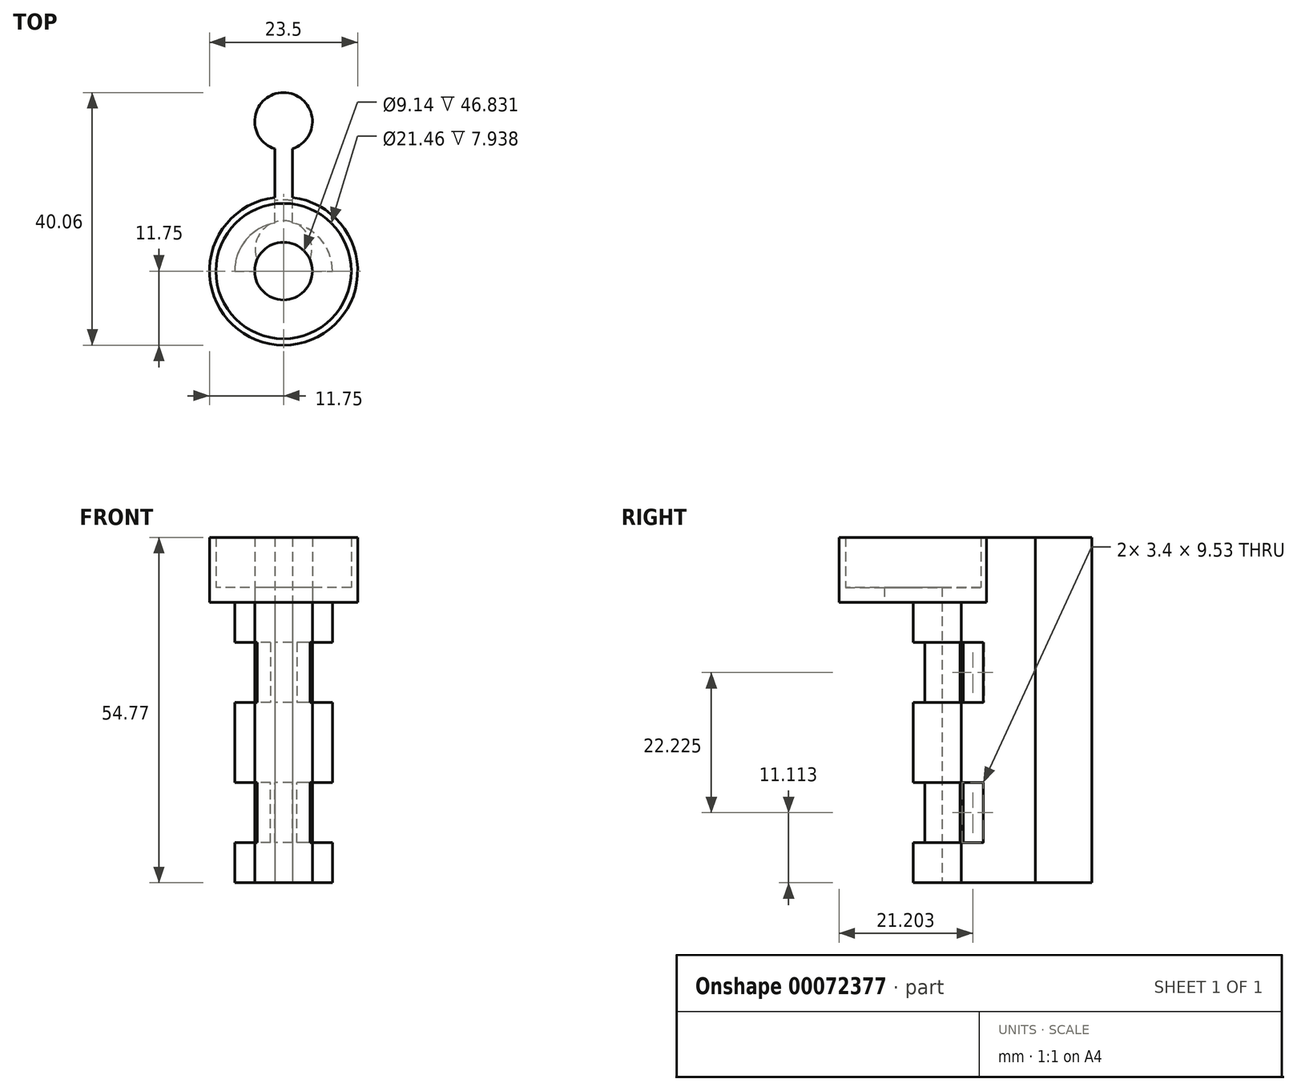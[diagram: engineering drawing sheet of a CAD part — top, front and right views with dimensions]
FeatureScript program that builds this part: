
annotation { "Feature Type Name" : "Feature", "Feature Type Description" : "" }
export const myFeature = defineFeature(function(context is Context, id is Id, definition is map)
    precondition{}
    {
        {
            var Q0;
            Q0=qCreatedBy(makeId("Top.planeOp"),FACE);
            var sketch = newSketch(context, id + "F0", { "sketchPlane" : qUnion([Q0])});
            skArc(sketch, "E0", {"start": v(4.57, 0) * mm, "mid": v(0, 4.57) * mm, "end": v(-4.57, 0) * mm});
            skArc(sketch, "E1", {"start": v(7.75, 0) * mm, "mid": v(0, 7.75) * mm, "end": v(-7.75, 0) * mm});
            skLineSegment(sketch, "E2", {"start": v(-7.75, 0) * mm, "end": v(-4.57, 0) * mm});
            skLineSegment(sketch, "E3", {"start": v(4.57, 0) * mm, "end": v(7.75, 0) * mm});
            skCircle(sketch, "E4", {"center": v(0, 23.73) * mm, "radius": 4.57 * mm});
            skLineSegment(sketch, "E5.rect.bottom", {"start": v(1.4, 7.62) * mm, "end": v(-1.4, 7.62) * mm, "construction": true});
            skLineSegment(sketch, "E5.rect.top", {"start": v(1.4, 19.38) * mm, "end": v(-1.4, 19.38) * mm, "construction": true});
            skLineSegment(sketch, "E5.rect.left", {"start": v(1.4, 7.62) * mm, "end": v(1.4, 19.38) * mm});
            skLineSegment(sketch, "E5.rect.right", {"start": v(-1.4, 7.62) * mm, "end": v(-1.4, 19.38) * mm});
            skPoint(sketch, "E5.rect.middle", {"position": v(0, 13.5) * mm});
            skSolve(sketch);
        }
        {
            var Q0;
            Q0 = qSketchRegion(id + "F0", true);
            extrude(context, id + "F1", {"entities" : qUnion([Q0]), "depth" : 44.45 * mm});
        }
        {
            var Q0;
            Q0=makeQuery(id+"F1.opExtrude","SWEPT_FACE",FACE,{"disambiguationData":[OSD([sQuery(id+"F0.wireOp",EDGE,"E5.rect.left")])]});
            var sketch = newSketch(context, id + "F2", { "sketchPlane" : qUnion([Q0])});
            skLineSegment(sketch, "E6.bottom", {"start": v(7.62, 3.18) * mm, "end": v(10.8, 3.18) * mm});
            skLineSegment(sketch, "E6.top", {"start": v(7.62, 12.7) * mm, "end": v(10.8, 12.7) * mm});
            skLineSegment(sketch, "E6.left", {"start": v(7.62, 3.17) * mm, "end": v(7.62, 12.7) * mm});
            skLineSegment(sketch, "E6.right", {"start": v(10.8, 3.18) * mm, "end": v(10.8, 12.7) * mm});
            skLineSegment(sketch, "E7.bottom", {"start": v(7.62, 31.75) * mm, "end": v(10.8, 31.75) * mm});
            skLineSegment(sketch, "E7.top", {"start": v(7.62, 41.28) * mm, "end": v(10.8, 41.28) * mm});
            skLineSegment(sketch, "E7.left", {"start": v(7.62, 31.75) * mm, "end": v(7.62, 41.28) * mm});
            skLineSegment(sketch, "E7.right", {"start": v(10.8, 31.75) * mm, "end": v(10.8, 41.28) * mm});
            skLineSegment(sketch, "E8", {"start": v(10.8, 41.28) * mm, "end": v(10.8, 44.45) * mm, "construction": true});
            skLineSegment(sketch, "E9", {"start": v(10.8, 3.18) * mm, "end": v(10.8, 0) * mm, "construction": true});
            skLineSegment(sketch, "E10.rect.bottom", {"start": v(2.38, 41.28) * mm, "end": v(-2.38, 41.28) * mm});
            skLineSegment(sketch, "E10.rect.top", {"start": v(2.38, 31.75) * mm, "end": v(-2.38, 31.75) * mm});
            skLineSegment(sketch, "E10.rect.left", {"start": v(2.38, 41.28) * mm, "end": v(2.38, 31.75) * mm});
            skLineSegment(sketch, "E10.rect.right", {"start": v(-2.38, 41.28) * mm, "end": v(-2.38, 31.75) * mm});
            skPoint(sketch, "E10.rect.middle", {"position": v(0, 36.51) * mm});
            skLineSegment(sketch, "E11.rect.bottom", {"start": v(2.38, 3.17) * mm, "end": v(-2.38, 3.17) * mm});
            skLineSegment(sketch, "E11.rect.top", {"start": v(2.38, 12.7) * mm, "end": v(-2.38, 12.7) * mm});
            skLineSegment(sketch, "E11.rect.left", {"start": v(2.38, 3.18) * mm, "end": v(2.38, 12.7) * mm});
            skLineSegment(sketch, "E11.rect.right", {"start": v(-2.38, 3.18) * mm, "end": v(-2.38, 12.7) * mm});
            skPoint(sketch, "E11.rect.middle", {"position": v(0, 7.94) * mm});
            skSolve(sketch);
        }
        {
            var Q0;
            Q0=qCreatedBy(makeId("Top.planeOp"),FACE);
            var sketch = newSketch(context, id + "F3", { "sketchPlane" : qUnion([Q0])});
            skCircle(sketch, "E12", {"center": v(0, 1.78) * mm, "radius": 2.8 * mm, "construction": true});
            skLineSegment(sketch, "E13", {"start": v(-2.68, 4.57) * mm, "end": v(4.01, 4.57) * mm, "construction": true});
            skLineSegment(sketch, "E14", {"start": v(-3.3, -1.02) * mm, "end": v(3.4, -1.02) * mm, "construction": true});
            skCircle(sketch, "E15", {"center": v(0, 3.48) * mm, "radius": 4.5 * mm});
            skCircle(sketch, "E16", {"center": v(0, 3.48) * mm, "radius": 7.8 * mm});
            skLineSegment(sketch, "E17.bottom", {"start": v(-8.86, 1.25) * mm, "end": v(11.53, 1.25) * mm});
            skLineSegment(sketch, "E17.top", {"start": v(-8.86, -6.45) * mm, "end": v(11.53, -6.45) * mm});
            skLineSegment(sketch, "E17.left", {"start": v(-8.86, 1.25) * mm, "end": v(-8.86, -6.45) * mm});
            skLineSegment(sketch, "E17.right", {"start": v(11.53, 1.25) * mm, "end": v(11.53, -6.45) * mm});
            skSolve(sketch);
        }
        {
            var Q0;
            Q0=qCreatedBy(makeId("Top.planeOp"),FACE);
            var Q1;
            Q1=makeQuery(id+"F1.opExtrude","CAP_FACE",FACE,{"disambiguationData":[OSD([sQuery(id+"F0.wireOp",EDGE,"E0"),sQuery(id+"F0.wireOp",EDGE,"E1"),sQuery(id+"F0.wireOp",EDGE,"E2"),sQuery(id+"F0.wireOp",EDGE,"E3"),sQuery(id+"F0.wireOp",EDGE,"E4"),sQuery(id+"F0.wireOp",EDGE,"E5.rect.left"),sQuery(id+"F0.wireOp",EDGE,"E5.rect.right")])],"isStart":false});
            cPlane(context, id + "F4", {"entities" : qUnion([Q0, Q1]), "cplaneType" : CPlaneType.MID_PLANE, "offset" : 152.4 * mm, "width" : 152.4 * mm, "height" : 152.4 * mm});
        }
        {
            var Q0;
            Q0=qCreatedBy(id+"F4.planeOp",FACE);
            cPlane(context, id + "F5", {"entities" : qUnion([Q0]), "cplaneType" : CPlaneType.OFFSET, "offset" : 6.35 * mm, "width" : 152.4 * mm, "height" : 152.4 * mm});
        }
        {
            var Q0;
            Q0=qCreatedBy(id+"F5.planeOp",FACE);
            var sketch = newSketch(context, id + "F6", { "sketchPlane" : qUnion([Q0])});
            skCircle(sketch, "E18", {"center": v(0, 3.48) * mm, "radius": 4.5 * mm});
            skCircle(sketch, "E19", {"center": v(0, 3.48) * mm, "radius": 7.8 * mm});
            skLineSegment(sketch, "E20.bottom", {"start": v(-8.42, 1.76) * mm, "end": v(11.76, 1.76) * mm});
            skLineSegment(sketch, "E20.top", {"start": v(-8.42, -6.32) * mm, "end": v(11.76, -6.32) * mm});
            skLineSegment(sketch, "E20.left", {"start": v(-8.42, 1.76) * mm, "end": v(-8.42, -6.32) * mm});
            skLineSegment(sketch, "E20.right", {"start": v(11.76, 1.76) * mm, "end": v(11.76, -6.32) * mm});
            skSolve(sketch);
        }
        {
            var Q0;
            Q0=qCreatedBy(id+"F4.planeOp",FACE);
            cPlane(context, id + "F7", {"entities" : qUnion([Q0]), "cplaneType" : CPlaneType.OFFSET, "offset" : 6.35 * mm, "oppositeDirection" : true, "width" : 152.4 * mm, "height" : 152.4 * mm});
        }
        {
            var Q0;
            Q0=qCreatedBy(id+"F7.planeOp",FACE);
            var sketch = newSketch(context, id + "F8", { "sketchPlane" : qUnion([Q0])});
            skCircle(sketch, "E21", {"center": v(0, 3.48) * mm, "radius": 4.5 * mm});
            skCircle(sketch, "E22", {"center": v(0, 3.48) * mm, "radius": 7.8 * mm});
            skLineSegment(sketch, "E23.bottom", {"start": v(-8.58, 1.82) * mm, "end": v(8.4, 1.82) * mm});
            skLineSegment(sketch, "E23.top", {"start": v(-8.58, -6) * mm, "end": v(8.4, -6) * mm});
            skLineSegment(sketch, "E23.left", {"start": v(-8.58, 1.82) * mm, "end": v(-8.58, -6) * mm});
            skLineSegment(sketch, "E23.right", {"start": v(8.4, 1.82) * mm, "end": v(8.4, -6) * mm});
            skSolve(sketch);
        }
        {
            var Q0;
            Q0=makeQuery(id+"F6.imprint","IMPRINT",FACE,{"disambiguationData":[TD([[makeQuery(id+"F6.imprint","IMPRINT",EDGE,{"derivedFrom":sQuery(id+"F6.wireOp",EDGE,"E18")}),-1.0]])]});
            var Q1;
            Q1=makeQuery(id+"F6.imprint","IMPRINT",FACE,{"disambiguationData":[TD([[makeQuery(id+"F6.imprint","IMPRINT",EDGE,{"derivedFrom":sQuery(id+"F6.wireOp",EDGE,"E20.top")}),1.0]])]});
            extrude(context, id + "F9", {"entities" : qUnion([Q0, Q1]), "operationType" : NewBodyOperationType.REMOVE, "depth" : 9.52 * mm});
        }
        {
            var Q0;
            Q0=makeQuery(id+"F8.imprint","IMPRINT",FACE,{"disambiguationData":[TD([[makeQuery(id+"F8.imprint","IMPRINT",EDGE,{"derivedFrom":sQuery(id+"F8.wireOp",EDGE,"E21")}),-1.0]])]});
            var Q1;
            Q1=makeQuery(id+"F8.imprint","IMPRINT",FACE,{"disambiguationData":[TD([[makeQuery(id+"F8.imprint","IMPRINT",EDGE,{"derivedFrom":sQuery(id+"F8.wireOp",EDGE,"E23.top")}),1.0]])]});
            extrude(context, id + "F10", {"entities" : qUnion([Q0, Q1]), "operationType" : NewBodyOperationType.REMOVE, "oppositeDirection" : true, "depth" : 9.52 * mm});
        }
        {
            var Q0;
            Q0=makeQuery(id+"F1.opExtrude","CAP_FACE",FACE,{"disambiguationData":[OSD([sQuery(id+"F0.wireOp",EDGE,"E0"),sQuery(id+"F0.wireOp",EDGE,"E1"),sQuery(id+"F0.wireOp",EDGE,"E2"),sQuery(id+"F0.wireOp",EDGE,"E3"),sQuery(id+"F0.wireOp",EDGE,"E4"),sQuery(id+"F0.wireOp",EDGE,"E5.rect.left"),sQuery(id+"F0.wireOp",EDGE,"E5.rect.right")])],"isStart":false});
            var sketch = newSketch(context, id + "F11", { "sketchPlane" : qUnion([Q0])});
            skCircle(sketch, "E24", {"center": v(0, 0) * mm, "radius": 11.75 * mm});
            skCircle(sketch, "E25", {"center": v(0, 0) * mm, "radius": 4.57 * mm});
            skSolve(sketch);
        }
        {
            var Q0;
            {var subQ0=sQuery(id+"F0.wireOp",EDGE,"E2");var subQ9=makeQuery(id+"F1.opExtrude","CAP_EDGE",EDGE,{"disambiguationData":[OSD([subQ0])],"isStart":false});Q0=makeQuery(id+"F11.imprint","IMPRINT",FACE,{"disambiguationData":[TD([[makeQuery(id+"F11.imprint","IMPRINT",EDGE,{"derivedFrom":subQ9}),-1.0]])]});}
            var Q1;
            {var subQ0=sQuery(id+"F0.wireOp",EDGE,"E2");var subQ9=makeQuery(id+"F1.opExtrude","CAP_EDGE",EDGE,{"disambiguationData":[OSD([subQ0])],"isStart":false});Q1=makeQuery(id+"F11.imprint","IMPRINT",FACE,{"disambiguationData":[TD([[makeQuery(id+"F11.imprint","IMPRINT",EDGE,{"derivedFrom":subQ9}),1.0]])]});}
            extrude(context, id + "F12", {"entities" : qUnion([Q0, Q1]), "operationType" : NewBodyOperationType.ADD, "depth" : 2.38 * mm});
        }
        {
            var Q0;
            Q0=makeQuery(id+"F12.opExtrude","CAP_FACE",FACE,{"disambiguationData":[OSD([sQuery(id+"F11.wireOp",EDGE,"E24"),sQuery(id+"F11.wireOp",EDGE,"E25")])],"isStart":false});
            var sketch = newSketch(context, id + "F13", { "sketchPlane" : qUnion([Q0])});
            skCircle(sketch, "E26", {"center": v(0, 0) * mm, "radius": 11.75 * mm});
            skCircle(sketch, "E27", {"center": v(0, 0) * mm, "radius": 10.73 * mm});
            skSolve(sketch);
        }
        {
            var Q0;
            Q0 = qSketchRegion(id + "F13", true);
            extrude(context, id + "F14", {"entities" : qUnion([Q0]), "operationType" : NewBodyOperationType.ADD, "depth" : 7.94 * mm});
        }
        {
            var Q0;
            Q0=makeQuery(id+"F1.opExtrude","CAP_FACE",FACE,{"disambiguationData":[OSD([sQuery(id+"F0.wireOp",EDGE,"E0"),sQuery(id+"F0.wireOp",EDGE,"E1"),sQuery(id+"F0.wireOp",EDGE,"E2"),sQuery(id+"F0.wireOp",EDGE,"E3"),sQuery(id+"F0.wireOp",EDGE,"E4"),sQuery(id+"F0.wireOp",EDGE,"E5.rect.left"),sQuery(id+"F0.wireOp",EDGE,"E5.rect.right")])],"isStart":false});
            var Q1;
            Q1=makeQuery(id+"F14.opExtrude","CAP_FACE",FACE,{"disambiguationData":[OSD([sQuery(id+"F13.wireOp",EDGE,"E26"),sQuery(id+"F13.wireOp",EDGE,"E27")])],"isStart":false});
            extrude(context, id + "F15", {"entities" : qUnion([Q0]), "operationType" : NewBodyOperationType.ADD, "endBound" : BoundingType.UP_TO_SURFACE, "endBoundEntityFace" : qUnion([Q1]), "depth" : 25.4 * mm});
        }
    });
